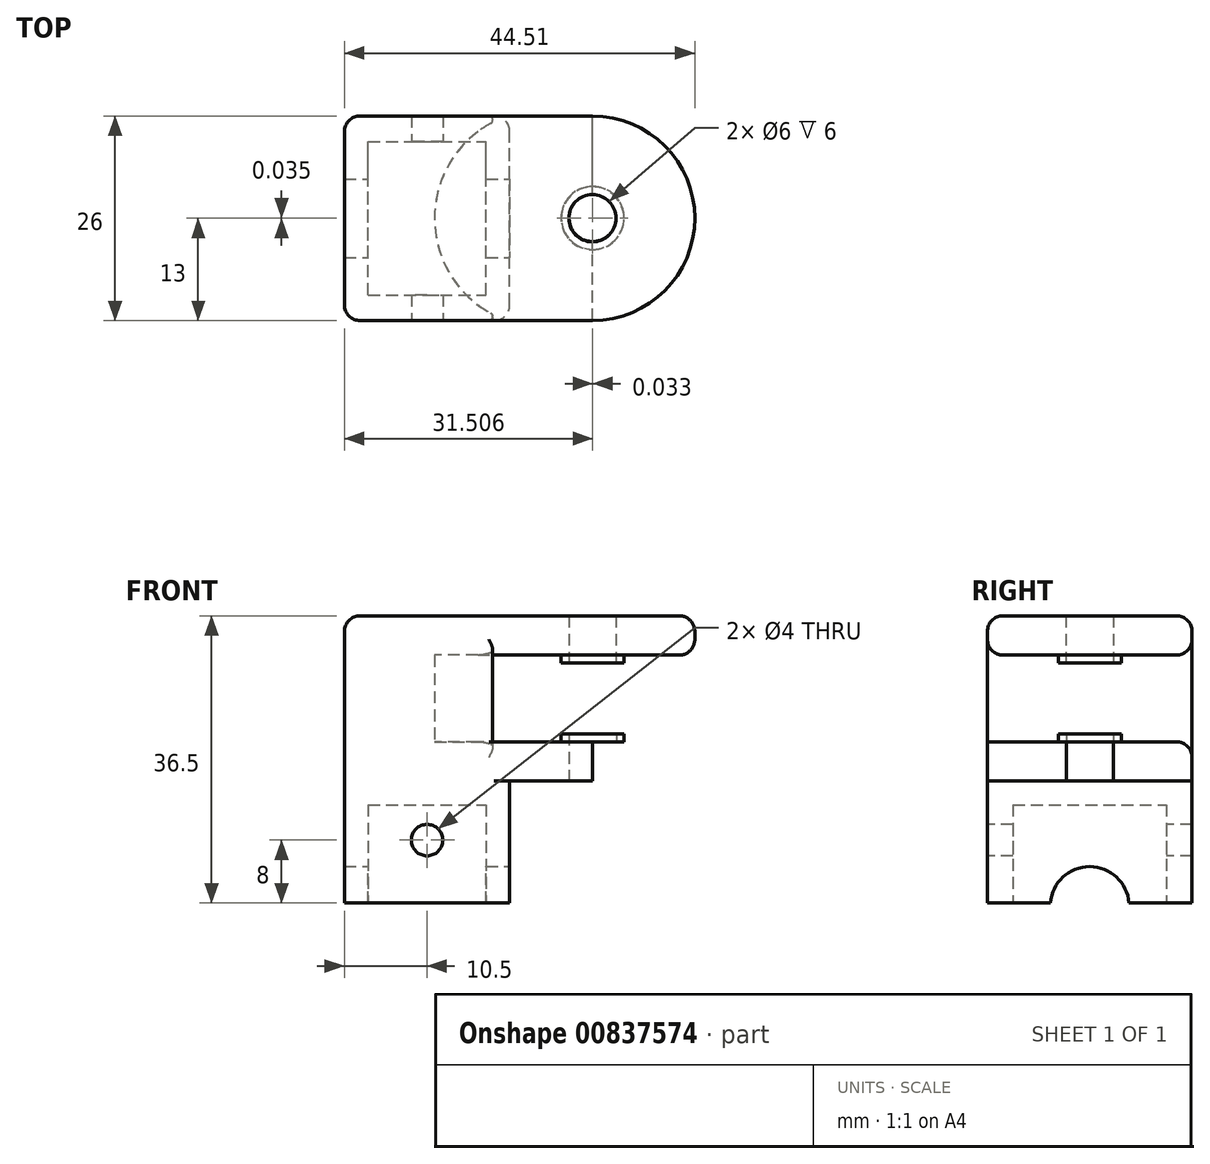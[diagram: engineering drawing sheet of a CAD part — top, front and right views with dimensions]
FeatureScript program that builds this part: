
annotation { "Feature Type Name" : "Feature", "Feature Type Description" : "" }
export const myFeature = defineFeature(function(context is Context, id is Id, definition is map)
    precondition{}
    {
        {
            var Q0;
            Q0=qCreatedBy(makeId("Top.planeOp"),FACE);
            var sketch = newSketch(context, id + "F0", { "sketchPlane" : qUnion([Q0])});
            skLineSegment(sketch, "E0.bottom", {"start": v(-7.5, -9.75) * mm, "end": v(7.5, -9.75) * mm});
            skLineSegment(sketch, "E0.top", {"start": v(-7.5, 9.75) * mm, "end": v(7.5, 9.75) * mm});
            skLineSegment(sketch, "E0.left", {"start": v(-7.5, -9.75) * mm, "end": v(-7.5, 9.75) * mm});
            skLineSegment(sketch, "E0.right", {"start": v(7.5, -9.75) * mm, "end": v(7.5, 9.75) * mm});
            skPoint(sketch, "E0.middle", {"position": v(0, 0) * mm});
            skLineSegment(sketch, "E1.bottom", {"start": v(-10.5, -13) * mm, "end": v(10.5, -13) * mm});
            skLineSegment(sketch, "E1.top", {"start": v(-10.5, 13) * mm, "end": v(10.5, 13) * mm});
            skLineSegment(sketch, "E1.left", {"start": v(-10.5, -13) * mm, "end": v(-10.5, 13) * mm});
            skLineSegment(sketch, "E1.right", {"start": v(10.5, -13) * mm, "end": v(10.5, 13) * mm});
            skSolve(sketch);
        }
        {
            var Q0;
            Q0=makeQuery(id+"F0.imprint","IMPRINT",FACE,{"disambiguationData":[TD([[makeQuery(id+"F0.imprint","IMPRINT",EDGE,{"derivedFrom":sQuery(id+"F0.wireOp",EDGE,"E0.bottom")}),-1.0]])]});
            extrude(context, id + "F1", {"entities" : qUnion([Q0]), "depth" : 12.5 * mm, "offsetDistance" : 25 * mm});
        }
        {
            var Q0;
            Q0=makeQuery(id+"F1.opExtrude","CAP_FACE",FACE,{"disambiguationData":[OSD([sQuery(id+"F0.wireOp",EDGE,"E0.bottom"),sQuery(id+"F0.wireOp",EDGE,"E0.top"),sQuery(id+"F0.wireOp",EDGE,"E0.left"),sQuery(id+"F0.wireOp",EDGE,"E0.right"),sQuery(id+"F0.wireOp",EDGE,"E1.bottom"),sQuery(id+"F0.wireOp",EDGE,"E1.top"),sQuery(id+"F0.wireOp",EDGE,"E1.left"),sQuery(id+"F0.wireOp",EDGE,"E1.right")])],"isStart":false});
            var sketch = newSketch(context, id + "F2", { "sketchPlane" : qUnion([Q0])});
            skLineSegment(sketch, "E2.bottom", {"start": v(-10.5, 13) * mm, "end": v(10.5, 13) * mm});
            skLineSegment(sketch, "E2.top", {"start": v(-10.5, -13) * mm, "end": v(10.5, -13) * mm});
            skLineSegment(sketch, "E2.left", {"start": v(-10.5, 13) * mm, "end": v(-10.5, -13) * mm});
            skLineSegment(sketch, "E2.right", {"start": v(10.5, 13) * mm, "end": v(10.5, -13) * mm});
            skPoint(sketch, "E2.middle", {"position": v(0, 0) * mm});
            skSolve(sketch);
        }
        {
            var Q0;
            Q0=makeQuery(id+"F2.imprint","IMPRINT",FACE,{"disambiguationData":[TD([[makeQuery(id+"F2.imprint","IMPRINT",EDGE,{"derivedFrom":sQuery(id+"F2.wireOp",EDGE,"E2.bottom")}),-1.0]])]});
            var Q1;
            Q1=makeQuery(id+"F2.imprint","IMPRINT",FACE,{"disambiguationData":[TD([[makeQuery(id+"F2.imprint","IMPRINT",EDGE,{"derivedFrom":makeQuery(id+"F1.opExtrude","CAP_EDGE",EDGE,{"disambiguationData":[OSD([sQuery(id+"F0.wireOp",EDGE,"E0.bottom")])],"isStart":false})}),1.0]])]});
            extrude(context, id + "F3", {"entities" : qUnion([Q0, Q1]), "operationType" : NewBodyOperationType.ADD, "depth" : 3 * mm, "offsetDistance" : 25 * mm});
        }
        {
            var Q0;
            Q0=makeQuery(id+"F3.opExtrude","CAP_FACE",FACE,{"disambiguationData":[OSD([sQuery(id+"F2.wireOp",EDGE,"E2.bottom"),sQuery(id+"F2.wireOp",EDGE,"E2.top"),sQuery(id+"F2.wireOp",EDGE,"E2.left"),sQuery(id+"F2.wireOp",EDGE,"E2.right")])],"isStart":false});
            var sketch = newSketch(context, id + "F4", { "sketchPlane" : qUnion([Q0])});
            skLineSegment(sketch, "E3", {"start": v(10.5, 13) * mm, "end": v(-10.5, 13) * mm});
            skLineSegment(sketch, "E4", {"start": v(-10.5, 13) * mm, "end": v(-10.5, -13) * mm});
            skLineSegment(sketch, "E5", {"start": v(-10.5, -13) * mm, "end": v(10.5, -13) * mm});
            skLineSegment(sketch, "E6.bottom", {"start": v(10.5, 13) * mm, "end": v(10.5, 13) * mm});
            skLineSegment(sketch, "E6.top", {"start": v(10.5, 11.49) * mm, "end": v(10.5, 11.49) * mm});
            skLineSegment(sketch, "E6.left", {"start": v(10.5, 13) * mm, "end": v(10.5, 11.49) * mm});
            skLineSegment(sketch, "E6.right", {"start": v(10.5, 13) * mm, "end": v(10.5, 11.49) * mm});
            skLineSegment(sketch, "E7.bottom", {"start": v(21.04, -13) * mm, "end": v(10.5, -13) * mm});
            skLineSegment(sketch, "E7.top", {"start": v(21.04, 13) * mm, "end": v(10.5, 13) * mm});
            skLineSegment(sketch, "E7.left", {"start": v(21.04, -13) * mm, "end": v(21.04, 13) * mm});
            skLineSegment(sketch, "E7.right", {"start": v(10.5, -13) * mm, "end": v(10.5, 13) * mm});
            skArc(sketch, "E8", {"start": v(21.04, 13) * mm, "mid": v(30.24, 9.2) * mm, "end": v(34.07, 0) * mm});
            skArc(sketch, "E9", {"start": v(21.04, -13) * mm, "mid": v(30.24, -9.2) * mm, "end": v(34.07, 0) * mm});
            skCircle(sketch, "E10", {"center": v(21.04, 0.04) * mm, "radius": 3 * mm});
            skSolve(sketch);
        }
        {
            var Q0;
            {var subQ4=sQuery(id+"F4.wireOp",EDGE,"E7.bottom");Q0=makeQuery(id+"F4.imprint","IMPRINT",FACE,{"disambiguationData":[TD([[makeQuery(id+"F4.imprint","IMPRINT",EDGE,{"derivedFrom":subQ4}),-1.0]])]});}
            var Q1;
            {var subQ1=sQuery(id+"F4.wireOp",EDGE,"E8");Q1=makeQuery(id+"F4.imprint","IMPRINT",FACE,{"disambiguationData":[TD([[makeQuery(id+"F4.imprint","IMPRINT",EDGE,{"derivedFrom":subQ1}),-1.0]])]});}
            var Q2;
            {var subQ3=sQuery(id+"F4.wireOp",EDGE,"E3");Q2=makeQuery(id+"F4.imprint","IMPRINT",FACE,{"disambiguationData":[TD([[makeQuery(id+"F4.imprint","IMPRINT",EDGE,{"derivedFrom":subQ3}),-1.0]])]});}
            extrude(context, id + "F5", {"entities" : qUnion([Q0, Q1, Q2]), "operationType" : NewBodyOperationType.ADD, "depth" : 5 * mm, "offsetDistance" : 25 * mm});
        }
        {
            var Q0;
            Q0=makeQuery(id+"F5.opExtrude","CAP_FACE",FACE,{"disambiguationData":[OSD([sQuery(id+"F4.wireOp",EDGE,"E3"),sQuery(id+"F4.wireOp",EDGE,"E4"),sQuery(id+"F4.wireOp",EDGE,"E5"),sQuery(id+"F4.wireOp",EDGE,"E7.bottom"),sQuery(id+"F4.wireOp",EDGE,"E7.top"),sQuery(id+"F4.wireOp",EDGE,"E8"),sQuery(id+"F4.wireOp",EDGE,"E9"),sQuery(id+"F4.wireOp",EDGE,"E10")])],"isStart":false});
            var sketch = newSketch(context, id + "F6", { "sketchPlane" : qUnion([Q0])});
            skCircle(sketch, "E11", {"center": v(21.04, 0.04) * mm, "radius": 3 * mm});
            skCircle(sketch, "E12", {"center": v(21.04, 0.04) * mm, "radius": 4 * mm});
            skSolve(sketch);
        }
        {
            var Q0;
            Q0=makeQuery(id+"F6.imprint","IMPRINT",FACE,{"disambiguationData":[TD([[makeQuery(id+"F6.imprint","IMPRINT",EDGE,{"derivedFrom":sQuery(id+"F6.wireOp",EDGE,"E11")}),-1.0]])]});
            extrude(context, id + "F7", {"entities" : qUnion([Q0]), "operationType" : NewBodyOperationType.ADD, "depth" : 1 * mm, "offsetDistance" : 25 * mm});
        }
        {
            var Q0;
            Q0=makeQuery(id+"F5.opExtrude","CAP_FACE",FACE,{"disambiguationData":[OSD([sQuery(id+"F4.wireOp",EDGE,"E3"),sQuery(id+"F4.wireOp",EDGE,"E4"),sQuery(id+"F4.wireOp",EDGE,"E5"),sQuery(id+"F4.wireOp",EDGE,"E7.bottom"),sQuery(id+"F4.wireOp",EDGE,"E7.top"),sQuery(id+"F4.wireOp",EDGE,"E8"),sQuery(id+"F4.wireOp",EDGE,"E9"),sQuery(id+"F4.wireOp",EDGE,"E10")])],"isStart":false});
            var sketch = newSketch(context, id + "F8", { "sketchPlane" : qUnion([Q0])});
            skArc(sketch, "E13", {"start": v(10.19, 13) * mm, "mid": v(0.96, 0) * mm, "end": v(10.19, -13) * mm});
            skLineSegment(sketch, "E14", {"start": v(10.19, 13) * mm, "end": v(-10.5, 13) * mm});
            skLineSegment(sketch, "E15", {"start": v(-10.5, 13) * mm, "end": v(-10.5, -13) * mm});
            skLineSegment(sketch, "E16", {"start": v(-10.5, -13) * mm, "end": v(10.19, -13) * mm});
            skSolve(sketch);
        }
        {
            var Q0;
            Q0=makeQuery(id+"F8.imprint","IMPRINT",FACE,{"disambiguationData":[TD([[makeQuery(id+"F8.imprint","IMPRINT",EDGE,{"derivedFrom":sQuery(id+"F8.wireOp",EDGE,"E13")}),-1.0]])]});
            extrude(context, id + "F9", {"entities" : qUnion([Q0]), "operationType" : NewBodyOperationType.ADD, "depth" : 11 * mm, "offsetDistance" : 25 * mm});
        }
        {
            var Q0;
            Q0=makeQuery(id+"F9.opExtrude","CAP_FACE",FACE,{"disambiguationData":[OSD([sQuery(id+"F8.wireOp",EDGE,"E13"),sQuery(id+"F8.wireOp",EDGE,"E14"),sQuery(id+"F8.wireOp",EDGE,"E15"),sQuery(id+"F8.wireOp",EDGE,"E16")])],"isStart":false});
            var sketch = newSketch(context, id + "F10", { "sketchPlane" : qUnion([Q0])});
            skLineSegment(sketch, "E17.bottom", {"start": v(-10.5, 13) * mm, "end": v(21, 13) * mm});
            skLineSegment(sketch, "E17.top", {"start": v(-10.5, -13.06) * mm, "end": v(21, -13.06) * mm});
            skLineSegment(sketch, "E17.left", {"start": v(-10.5, 13) * mm, "end": v(-10.5, -13.06) * mm});
            skLineSegment(sketch, "E17.right", {"start": v(21, 0) * mm, "end": v(21, -0.03) * mm});
            skArc(sketch, "E18", {"start": v(21, -13) * mm, "mid": v(34, 0) * mm, "end": v(21, 13) * mm});
            skPoint(sketch, "E18.centerSnap0", {"position": v(21, -0.03) * mm});
            skLineSegment(sketch, "E19.trimOffspring", {"start": v(21, -13) * mm, "end": v(21, -13.06) * mm});
            skCircle(sketch, "E20", {"center": v(21, 0) * mm, "radius": 3 * mm});
            skLineSegment(sketch, "E21", {"start": v(21, 13) * mm, "end": v(-10.5, 13) * mm});
            skLineSegment(sketch, "E22", {"start": v(-10.5, -13) * mm, "end": v(21, -13) * mm});
            skSolve(sketch);
        }
        {
            var Q0;
            {var subQ2=sQuery(id+"F10.wireOp",EDGE,"E18");Q0=makeQuery(id+"F10.imprint","IMPRINT",FACE,{"disambiguationData":[TD([[makeQuery(id+"F10.imprint","IMPRINT",EDGE,{"derivedFrom":subQ2}),1.0]])]});}
            var Q1;
            {var subQ5=makeQuery(id+"F9.opExtrude","CAP_EDGE",EDGE,{"disambiguationData":[OSD([sQuery(id+"F8.wireOp",EDGE,"E13")])],"isStart":false});Q1=makeQuery(id+"F10.imprint","IMPRINT",FACE,{"disambiguationData":[TD([[makeQuery(id+"F10.imprint","IMPRINT",EDGE,{"derivedFrom":subQ5}),-1.0]])]});}
            extrude(context, id + "F11", {"entities" : qUnion([Q0, Q1]), "operationType" : NewBodyOperationType.ADD, "depth" : 5 * mm, "offsetDistance" : 25 * mm});
        }
        {
            var Q0;
            Q0=makeQuery(id+"F11.opExtrude","CAP_FACE",FACE,{"disambiguationData":[OSD([sQuery(id+"F10.wireOp",EDGE,"E17.left"),sQuery(id+"F10.wireOp",EDGE,"E18"),sQuery(id+"F10.wireOp",EDGE,"E20"),sQuery(id+"F10.wireOp",EDGE,"E21"),sQuery(id+"F10.wireOp",EDGE,"E22")])],"isStart":false});
            var sketch = newSketch(context, id + "F12", { "sketchPlane" : qUnion([Q0])});
            skCircle(sketch, "E23", {"center": v(21, 0) * mm, "radius": 3 * mm});
            skCircle(sketch, "E24", {"center": v(21, 0) * mm, "radius": 4 * mm});
            skSolve(sketch);
        }
        {
            var Q0;
            Q0=makeQuery(id+"F12.imprint","IMPRINT",FACE,{"disambiguationData":[TD([[makeQuery(id+"F12.imprint","IMPRINT",EDGE,{"derivedFrom":sQuery(id+"F12.wireOp",EDGE,"E23")}),-1.0]])]});
            extrude(context, id + "F13", {"entities" : qUnion([Q0]), "operationType" : NewBodyOperationType.ADD, "oppositeDirection" : true, "depth" : 6 * mm, "offsetDistance" : 25 * mm});
        }
        {
            var Q0;
            Q0=makeQuery(id+"F11.boolean.opBoolean","MERGE",EDGE,{"derivedFrom":[makeQuery(id+"F9.boolean.opBoolean","MERGE",EDGE,{"derivedFrom":[makeQuery(id+"F5.boolean.opBoolean","MERGE",EDGE,{"derivedFrom":[makeQuery(id+"F3.boolean.opBoolean","MERGE",EDGE,{"derivedFrom":[makeQuery(id+"F1.opExtrude","SWEPT_EDGE",EDGE,{"disambiguationData":[OSD([sQuery(id+"F0.wireOp",EDGE,"E1.bottom"),sQuery(id+"F0.wireOp",EDGE,"E1.left")])]}),makeQuery(id+"F3.opExtrude","SWEPT_EDGE",EDGE,{"disambiguationData":[OSD([sQuery(id+"F2.wireOp",EDGE,"E2.top"),sQuery(id+"F2.wireOp",EDGE,"E2.left")])]})]}),makeQuery(id+"F5.opExtrude","SWEPT_EDGE",EDGE,{"disambiguationData":[OSD([sQuery(id+"F4.wireOp",EDGE,"E4"),sQuery(id+"F4.wireOp",EDGE,"E5")])]})]}),makeQuery(id+"F9.opExtrude","SWEPT_EDGE",EDGE,{"disambiguationData":[OSD([sQuery(id+"F8.wireOp",EDGE,"E15"),sQuery(id+"F8.wireOp",EDGE,"E16")])]})]}),makeQuery(id+"F11.opExtrude","SWEPT_EDGE",EDGE,{"disambiguationData":[OSD([sQuery(id+"F10.wireOp",EDGE,"E17.left"),sQuery(id+"F10.wireOp",EDGE,"E22")])]})]});
            var Q1;
            Q1=makeQuery(id+"F11.boolean.opBoolean","MERGE",EDGE,{"derivedFrom":[makeQuery(id+"F9.boolean.opBoolean","MERGE",EDGE,{"derivedFrom":[makeQuery(id+"F5.boolean.opBoolean","MERGE",EDGE,{"derivedFrom":[makeQuery(id+"F3.boolean.opBoolean","MERGE",EDGE,{"derivedFrom":[makeQuery(id+"F1.opExtrude","SWEPT_EDGE",EDGE,{"disambiguationData":[OSD([sQuery(id+"F0.wireOp",EDGE,"E1.top"),sQuery(id+"F0.wireOp",EDGE,"E1.left")])]}),makeQuery(id+"F3.opExtrude","SWEPT_EDGE",EDGE,{"disambiguationData":[OSD([sQuery(id+"F2.wireOp",EDGE,"E2.bottom"),sQuery(id+"F2.wireOp",EDGE,"E2.left")])]})]}),makeQuery(id+"F5.opExtrude","SWEPT_EDGE",EDGE,{"disambiguationData":[OSD([sQuery(id+"F4.wireOp",EDGE,"E3"),sQuery(id+"F4.wireOp",EDGE,"E4")])]})]}),makeQuery(id+"F9.opExtrude","SWEPT_EDGE",EDGE,{"disambiguationData":[OSD([sQuery(id+"F8.wireOp",EDGE,"E14"),sQuery(id+"F8.wireOp",EDGE,"E15")])]})]}),makeQuery(id+"F11.opExtrude","SWEPT_EDGE",EDGE,{"disambiguationData":[OSD([sQuery(id+"F10.wireOp",EDGE,"E17.left"),sQuery(id+"F10.wireOp",EDGE,"E21")])]})]});
            var Q2;
            Q2=makeQuery(id+"F3.boolean.opBoolean","MERGE",EDGE,{"derivedFrom":[makeQuery(id+"F1.opExtrude","SWEPT_EDGE",EDGE,{"disambiguationData":[OSD([sQuery(id+"F0.wireOp",EDGE,"E1.top"),sQuery(id+"F0.wireOp",EDGE,"E1.right")])]}),makeQuery(id+"F3.opExtrude","SWEPT_EDGE",EDGE,{"disambiguationData":[OSD([sQuery(id+"F2.wireOp",EDGE,"E2.bottom"),sQuery(id+"F2.wireOp",EDGE,"E2.right")])]})]});
            var Q3;
            Q3=makeQuery(id+"F3.boolean.opBoolean","MERGE",EDGE,{"derivedFrom":[makeQuery(id+"F1.opExtrude","SWEPT_EDGE",EDGE,{"disambiguationData":[OSD([sQuery(id+"F0.wireOp",EDGE,"E1.bottom"),sQuery(id+"F0.wireOp",EDGE,"E1.right")])]}),makeQuery(id+"F3.opExtrude","SWEPT_EDGE",EDGE,{"disambiguationData":[OSD([sQuery(id+"F2.wireOp",EDGE,"E2.top"),sQuery(id+"F2.wireOp",EDGE,"E2.right")])]})]});
            var Q4;
            Q4=makeQuery(id+"F11.opExtrude","CAP_EDGE",EDGE,{"disambiguationData":[OSD([sQuery(id+"F10.wireOp",EDGE,"E17.left")])],"isStart":false});
            var Q5;
            Q5=makeQuery(id+"F11.opExtrude","CAP_EDGE",EDGE,{"disambiguationData":[OSD([sQuery(id+"F10.wireOp",EDGE,"E22")])],"isStart":false});
            var Q6;
            Q6=makeQuery(id+"F11.opExtrude","CAP_EDGE",EDGE,{"disambiguationData":[OSD([sQuery(id+"F10.wireOp",EDGE,"E21")])],"isStart":false});
            var Q7;
            Q7=makeQuery(id+"F5.opExtrude","CAP_EDGE",EDGE,{"disambiguationData":[OSD([sQuery(id+"F4.wireOp",EDGE,"E3"),sQuery(id+"F4.wireOp",EDGE,"E7.top")])],"isStart":false});
            var Q8;
            Q8=makeQuery(id+"F5.opExtrude","CAP_EDGE",EDGE,{"disambiguationData":[OSD([sQuery(id+"F4.wireOp",EDGE,"E9")])],"isStart":false});
            var Q9;
            Q9=makeQuery(id+"F5.opExtrude","CAP_EDGE",EDGE,{"disambiguationData":[OSD([sQuery(id+"F4.wireOp",EDGE,"E9")])],"isStart":true});
            var Q10;
            Q10=makeQuery(id+"F11.opExtrude","CAP_EDGE",EDGE,{"disambiguationData":[OSD([sQuery(id+"F10.wireOp",EDGE,"E18")])],"isStart":true});
            fillet(context, id + "F14", {"entities" : qUnion([Q0, Q1, Q2, Q3, Q4, Q5, Q6, Q7, Q8, Q9, Q10]), "radius" : 2 * mm, "tangentPropagation" : true, "allowEdgeOverflow" : false});
        }
        {
            var Q0;
            Q0=makeQuery(id+"F9.opExtrude","SWEPT_EDGE",EDGE,{"disambiguationData":[OSD([sQuery(id+"F4.wireOp",EDGE,"E3"),sQuery(id+"F4.wireOp",EDGE,"E7.top"),sQuery(id+"F8.wireOp",EDGE,"E13"),sQuery(id+"F8.wireOp",EDGE,"E14")])]});
            var Q1;
            Q1=makeQuery(id+"F9.opExtrude","SWEPT_EDGE",EDGE,{"disambiguationData":[OSD([sQuery(id+"F4.wireOp",EDGE,"E5"),sQuery(id+"F4.wireOp",EDGE,"E7.bottom"),sQuery(id+"F8.wireOp",EDGE,"E13"),sQuery(id+"F8.wireOp",EDGE,"E16")])]});
            fillet(context, id + "F15", {"entities" : qUnion([Q0, Q1]), "radius" : 0.5 * mm, "tangentPropagation" : true, "allowEdgeOverflow" : false});
        }
        {
            var Q0;
            Q0=makeQuery(id+"F3.boolean.opBoolean","MERGE",FACE,{"derivedFrom":[makeQuery(id+"F1.opExtrude","SWEPT_FACE",FACE,{"disambiguationData":[OSD([sQuery(id+"F0.wireOp",EDGE,"E1.right")])]}),makeQuery(id+"F3.opExtrude","SWEPT_FACE",FACE,{"disambiguationData":[OSD([sQuery(id+"F2.wireOp",EDGE,"E2.right")])]})]});
            var sketch = newSketch(context, id + "F16", { "sketchPlane" : qUnion([Q0])});
            skCircle(sketch, "E25", {"center": v(0, -0.36) * mm, "radius": 5 * mm});
            skSolve(sketch);
        }
        {
            var Q0;
            {var subQ0=sQuery(id+"F16.wireOp",EDGE,"E25");var subQ1=makeQuery(id+"F1.opExtrude","CAP_EDGE",EDGE,{"disambiguationData":[OSD([sQuery(id+"F0.wireOp",EDGE,"E1.right")])],"isStart":true});var subQ2=makeQuery(id+"F16.imprint","INTERSECT",VERTEX,{"disambiguationData":[OD(0.0)],"derivedFrom":[subQ1,subQ0]});Q0=makeQuery(id+"F16.imprint","IMPRINT",FACE,{"disambiguationData":[TD([[makeQuery(id+"F16.imprint","IMPRINT",EDGE,{"disambiguationData":[TD([[subQ2,1.0]])],"derivedFrom":subQ0}),1.0]])]});}
            extrude(context, id + "F17", {"entities" : qUnion([Q0]), "operationType" : NewBodyOperationType.REMOVE, "oppositeDirection" : true, "depth" : 25 * mm, "offsetDistance" : 25 * mm});
        }
        {
            var Q0;
            Q0=makeQuery(id+"F11.boolean.opBoolean","MERGE",FACE,{"derivedFrom":[makeQuery(id+"F9.boolean.opBoolean","MERGE",FACE,{"derivedFrom":[makeQuery(id+"F5.boolean.opBoolean","MERGE",FACE,{"derivedFrom":[makeQuery(id+"F3.boolean.opBoolean","MERGE",FACE,{"derivedFrom":[makeQuery(id+"F1.opExtrude","SWEPT_FACE",FACE,{"disambiguationData":[OSD([sQuery(id+"F0.wireOp",EDGE,"E1.bottom")])]}),makeQuery(id+"F3.opExtrude","SWEPT_FACE",FACE,{"disambiguationData":[OSD([sQuery(id+"F2.wireOp",EDGE,"E2.top")])]})]}),makeQuery(id+"F5.opExtrude","SWEPT_FACE",FACE,{"disambiguationData":[OSD([sQuery(id+"F4.wireOp",EDGE,"E5"),sQuery(id+"F4.wireOp",EDGE,"E7.bottom")])]})]}),makeQuery(id+"F9.opExtrude","SWEPT_FACE",FACE,{"disambiguationData":[OSD([sQuery(id+"F8.wireOp",EDGE,"E16")])]})]}),makeQuery(id+"F11.opExtrude","SWEPT_FACE",FACE,{"disambiguationData":[OSD([sQuery(id+"F10.wireOp",EDGE,"E22")])]})]});
            var sketch = newSketch(context, id + "F18", { "sketchPlane" : qUnion([Q0])});
            skCircle(sketch, "E26", {"center": v(0, 8) * mm, "radius": 2 * mm});
            skSolve(sketch);
        }
        {
            var Q0;
            Q0=makeQuery(id+"F18.imprint","IMPRINT",FACE,{"disambiguationData":[TD([[makeQuery(id+"F18.imprint","IMPRINT",EDGE,{"derivedFrom":sQuery(id+"F18.wireOp",EDGE,"E26")}),1.0]])]});
            extrude(context, id + "F19", {"entities" : qUnion([Q0]), "operationType" : NewBodyOperationType.REMOVE, "oppositeDirection" : true, "depth" : 44.7 * mm, "offsetDistance" : 25 * mm});
        }
    });
